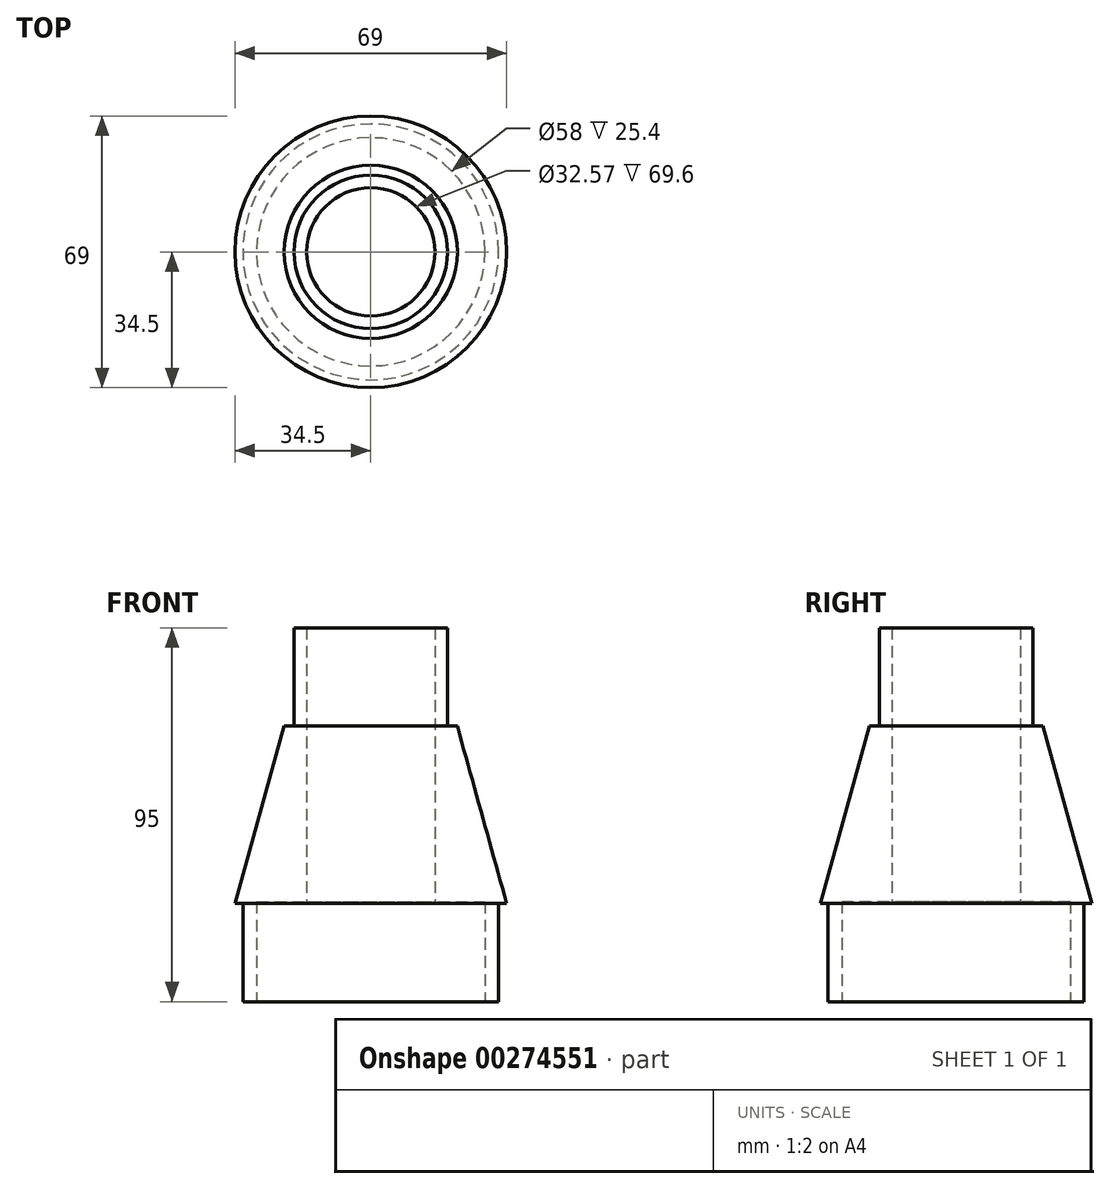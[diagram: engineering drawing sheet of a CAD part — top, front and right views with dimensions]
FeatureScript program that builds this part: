
annotation { "Feature Type Name" : "Feature", "Feature Type Description" : "" }
export const myFeature = defineFeature(function(context is Context, id is Id, definition is map)
    precondition{}
    {
        {
            var Q0;
            Q0=qCreatedBy(makeId("Front.planeOp"),FACE);
            var sketch = newSketch(context, id + "F0", { "sketchPlane" : qUnion([Q0])});
            skLineSegment(sketch, "E0", {"start": v(0, 0) * mm, "end": v(-34.5, 0) * mm});
            skLineSegment(sketch, "E1", {"start": v(-34.5, 0) * mm, "end": v(-22, 45) * mm});
            skLineSegment(sketch, "E2", {"start": v(-22, 45) * mm, "end": v(0, 45) * mm});
            skLineSegment(sketch, "E3", {"start": v(0, 45) * mm, "end": v(0, 0) * mm});
            skSolve(sketch);
        }
        {
            var Q0;
            Q0=makeQuery(id+"F0.imprint","IMPRINT",FACE,{"disambiguationData":[TD([[makeQuery(id+"F0.imprint","IMPRINT",EDGE,{"derivedFrom":sQuery(id+"F0.wireOp",EDGE,"E0")}),-1.0]])]});
            var Q1;
            Q1=sQuery(id+"F0.wireOp",EDGE,"E3");
            revolve(context, id + "F1", {"entities" : qUnion([Q0]), "axis" : qUnion([Q1]), "revolveType" : RevolveType.FULL});
        }
        {
            var Q0;
            Q0=makeQuery(id+"F1.opRevolve","SWEPT_FACE",FACE,{"disambiguationData":[OSD([sQuery(id+"F0.wireOp",EDGE,"E0")])]});
            var sketch = newSketch(context, id + "F2", { "sketchPlane" : qUnion([Q0])});
            skCircle(sketch, "E4", {"center": v(0, 0) * mm, "radius": 32.5 * mm});
            skSolve(sketch);
        }
        {
            var Q0;
            Q0=makeQuery(id+"F1.opRevolve","SWEPT_FACE",FACE,{"disambiguationData":[OSD([sQuery(id+"F0.wireOp",EDGE,"E2")])]});
            var sketch = newSketch(context, id + "F3", { "sketchPlane" : qUnion([Q0])});
            skCircle(sketch, "E5", {"center": v(0, 0) * mm, "radius": 19.5 * mm});
            skSolve(sketch);
        }
        {
            var Q0;
            Q0 = qSketchRegion(id + "F2", true);
            extrude(context, id + "F4", {"entities" : qUnion([Q0]), "operationType" : NewBodyOperationType.ADD, "depth" : 25 * mm});
        }
        {
            var Q0;
            Q0=makeQuery(id+"F4.opExtrude","CAP_FACE",FACE,{"disambiguationData":[OSD([sQuery(id+"F2.wireOp",EDGE,"E4")])],"isStart":false});
            var sketch = newSketch(context, id + "F5", { "sketchPlane" : qUnion([Q0])});
            skCircle(sketch, "E6", {"center": v(0, 0) * mm, "radius": 29 * mm});
            skSolve(sketch);
        }
        {
            var Q0;
            Q0 = qSketchRegion(id + "F5", true);
            extrude(context, id + "F6", {"entities" : qUnion([Q0]), "operationType" : NewBodyOperationType.REMOVE, "oppositeDirection" : true, "depth" : 25.4 * mm});
        }
        {
            var Q0;
            Q0=makeQuery(id+"F6.boolean.opBoolean","COPY",FACE,{"derivedFrom":makeQuery(id+"F6.opExtrude","CAP_FACE",FACE,{"disambiguationData":[OSD([sQuery(id+"F5.wireOp",EDGE,"E6")])],"isStart":false})});
            var sketch = newSketch(context, id + "F7", { "sketchPlane" : qUnion([Q0])});
            skCircle(sketch, "E7", {"center": v(0, 0) * mm, "radius": 14.37 * mm});
            skSolve(sketch);
        }
        {
            var Q0;
            Q0 = qSketchRegion(id + "F3", true);
            var Q1;
            Q1=sQuery(id+"F3.wireOp",EDGE,"E5");
            extrude(context, id + "F8", {"entities" : qUnion([Q0]), "operationType" : NewBodyOperationType.ADD, "surfaceEntities" : qUnion([Q1]), "depth" : 25 * mm});
        }
        {
            var Q0;
            Q0=makeQuery(id+"F7.imprint","IMPRINT",FACE,{"disambiguationData":[TD([[makeQuery(id+"F7.imprint","IMPRINT",EDGE,{"derivedFrom":sQuery(id+"F7.wireOp",EDGE,"E7")}),-1.0]])]});
            var sketch = newSketch(context, id + "F9", { "sketchPlane" : qUnion([Q0])});
            skCircle(sketch, "E8", {"center": v(0, 0) * mm, "radius": 16.29 * mm});
            skSolve(sketch);
        }
        {
            var Q0;
            Q0 = qSketchRegion(id + "F9", true);
            extrude(context, id + "F10", {"entities" : qUnion([Q0]), "operationType" : NewBodyOperationType.REMOVE, "oppositeDirection" : true, "depth" : 121 * mm});
        }
        {
            var Q0;
            Q0=sQuery(id+"F0.wireOp",EDGE,"E3");
            cPoint(context, id + "F11", {"entities" : qUnion([Q0]), "parameter" : 0.5});
        }
        {
            var Q0;
            Q0=makeQuery(id+"F1.opRevolve","SWEPT_BODY",BODY,{"disambiguationData":[OSD([sQuery(id+"F0.wireOp",EDGE,"E0"),sQuery(id+"F0.wireOp",EDGE,"E1"),sQuery(id+"F0.wireOp",EDGE,"E2"),sQuery(id+"F0.wireOp",EDGE,"E3")])]});
            var Q1;
            Q1 = qCreatedBy(id + "F11" ,VERTEX);
            var Q2;
            Q2=makeQuery(id+"F1.opRevolve","SWEPT_FACE",FACE,{"disambiguationData":[OSD([sQuery(id+"F0.wireOp",EDGE,"E1")])]});
            var Q3;
            Q3=makeQuery(id+"F10.boolean.opBoolean","COPY",FACE,{"derivedFrom":makeQuery(id+"F10.opExtrude","SWEPT_FACE",FACE,{"disambiguationData":[OSD([sQuery(id+"F9.wireOp",EDGE,"E8")])]})});
            transform(context, id + "F12", {"entities" : qUnion([Q0]), "transformType" : TransformType.TRANSLATION_DISTANCE, "transformDirection" : qUnion([Q2, Q3]), "distance" : 25 * mm, "oppositeDirection" : true, "makeCopy" : false});
        }
    });
